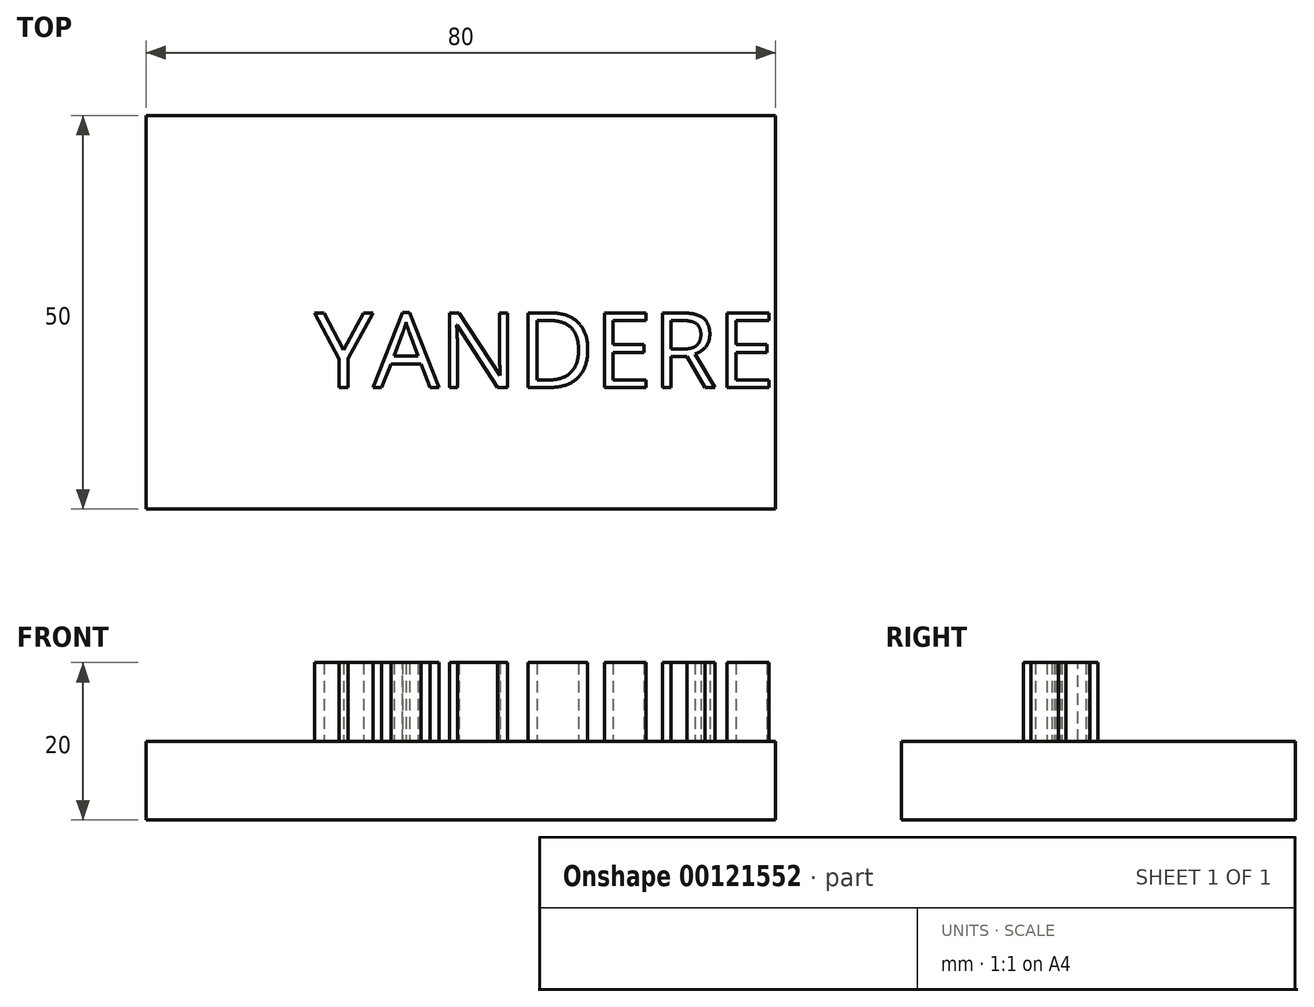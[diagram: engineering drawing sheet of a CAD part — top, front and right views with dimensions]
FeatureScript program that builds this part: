
annotation { "Feature Type Name" : "Feature", "Feature Type Description" : "" }
export const myFeature = defineFeature(function(context is Context, id is Id, definition is map)
    precondition{}
    {
        {
            var Q0;
            Q0=qCreatedBy(makeId("Top.planeOp"),FACE);
            var sketch = newSketch(context, id + "F0", { "sketchPlane" : qUnion([Q0])});
            skLineSegment(sketch, "E0.bottom", {"start": v(40, 25) * mm, "end": v(-40, 25) * mm});
            skLineSegment(sketch, "E0.top", {"start": v(40, -25) * mm, "end": v(-40, -25) * mm});
            skLineSegment(sketch, "E0.left", {"start": v(40, 25) * mm, "end": v(40, -25) * mm});
            skLineSegment(sketch, "E0.right", {"start": v(-40, 25) * mm, "end": v(-40, -25) * mm});
            skPoint(sketch, "E0.middle", {"position": v(0, 0) * mm});
            skSolve(sketch);
        }
        {
            var Q0;
            Q0 = qSketchRegion(id + "F0", true);
            extrude(context, id + "F1", {"entities" : qUnion([Q0]), "depth" : 10 * mm});
        }
        {
            var Q0;
            Q0=makeQuery(id+"F1.opExtrude","CAP_FACE",FACE,{"disambiguationData":[OSD([sQuery(id+"F0.wireOp",EDGE,"E0.bottom"),sQuery(id+"F0.wireOp",EDGE,"E0.top"),sQuery(id+"F0.wireOp",EDGE,"E0.left"),sQuery(id+"F0.wireOp",EDGE,"E0.right")])],"isStart":false});
            var sketch = newSketch(context, id + "F2", { "sketchPlane" : qUnion([Q0])});
            skText(sketch, "E1", { "text": "YANDERE", "fontName": "OpenSans-Regular.ttf"});
            const initialGuessF2  = {"E1": [-0.01859, -0.00956, 1, 0, 0.00956]};
            skSetInitialGuess(sketch, initialGuessF2);
            skSolve(sketch);
        }
        {
            var Q0;
            Q0 = qSketchRegion(id + "F2", true);
            extrude(context, id + "F3", {"entities" : qUnion([Q0]), "operationType" : NewBodyOperationType.ADD, "depth" : 10 * mm});
        }
    });
